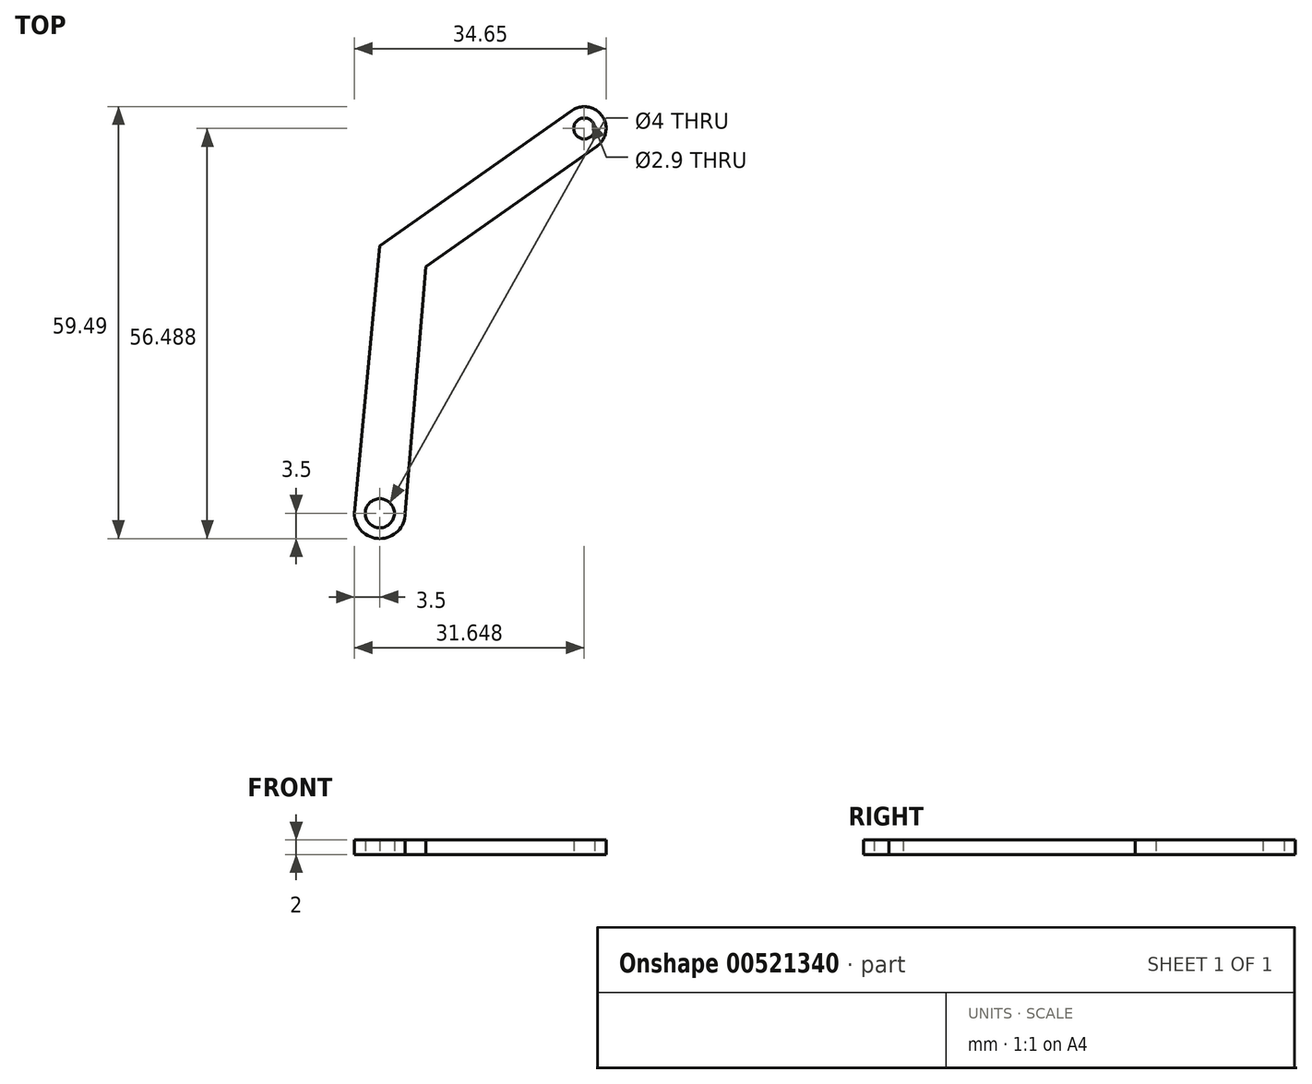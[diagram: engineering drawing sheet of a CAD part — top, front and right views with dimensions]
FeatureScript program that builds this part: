
annotation { "Feature Type Name" : "Feature", "Feature Type Description" : "" }
export const myFeature = defineFeature(function(context is Context, id is Id, definition is map)
    precondition{}
    {
        {
            var Q0;
            Q0=qCreatedBy(makeId("Top.planeOp"),FACE);
            var sketch = newSketch(context, id + "F0", { "sketchPlane" : qUnion([Q0])});
            skCircle(sketch, "E0", {"center": v(0, 0) * mm, "radius": 2 * mm});
            skArc(sketch, "E1", {"start": v(3.5, 0) * mm, "mid": v(0, -3.5) * mm, "end": v(-3.5, 0) * mm});
            skLineSegment(sketch, "E2", {"start": v(-3.5, 0) * mm, "end": v(0, 36.8) * mm});
            skLineSegment(sketch, "E3", {"start": v(0, 36.8) * mm, "end": v(26.42, 55.44) * mm});
            skLineSegment(sketch, "E4", {"start": v(26.42, 55.44) * mm, "end": v(29.88, 50.54) * mm, "construction": true});
            skLineSegment(sketch, "E5", {"start": v(29.88, 50.54) * mm, "end": v(6.36, 33.95) * mm});
            skLineSegment(sketch, "E6", {"start": v(6.36, 33.95) * mm, "end": v(3.5, 0) * mm});
            skArc(sketch, "E7", {"start": v(26.42, 55.44) * mm, "mid": v(30.6, 54.72) * mm, "end": v(29.88, 50.54) * mm});
            skCircle(sketch, "E8", {"center": v(28.15, 52.99) * mm, "radius": 1.45 * mm});
            skSolve(sketch);
        }
        {
            var Q0;
            Q0 = qSketchRegion(id + "F0", true);
            extrude(context, id + "F1", {"entities" : qUnion([Q0]), "depth" : 2 * mm, "offsetDistance" : 25 * mm});
        }
    });
